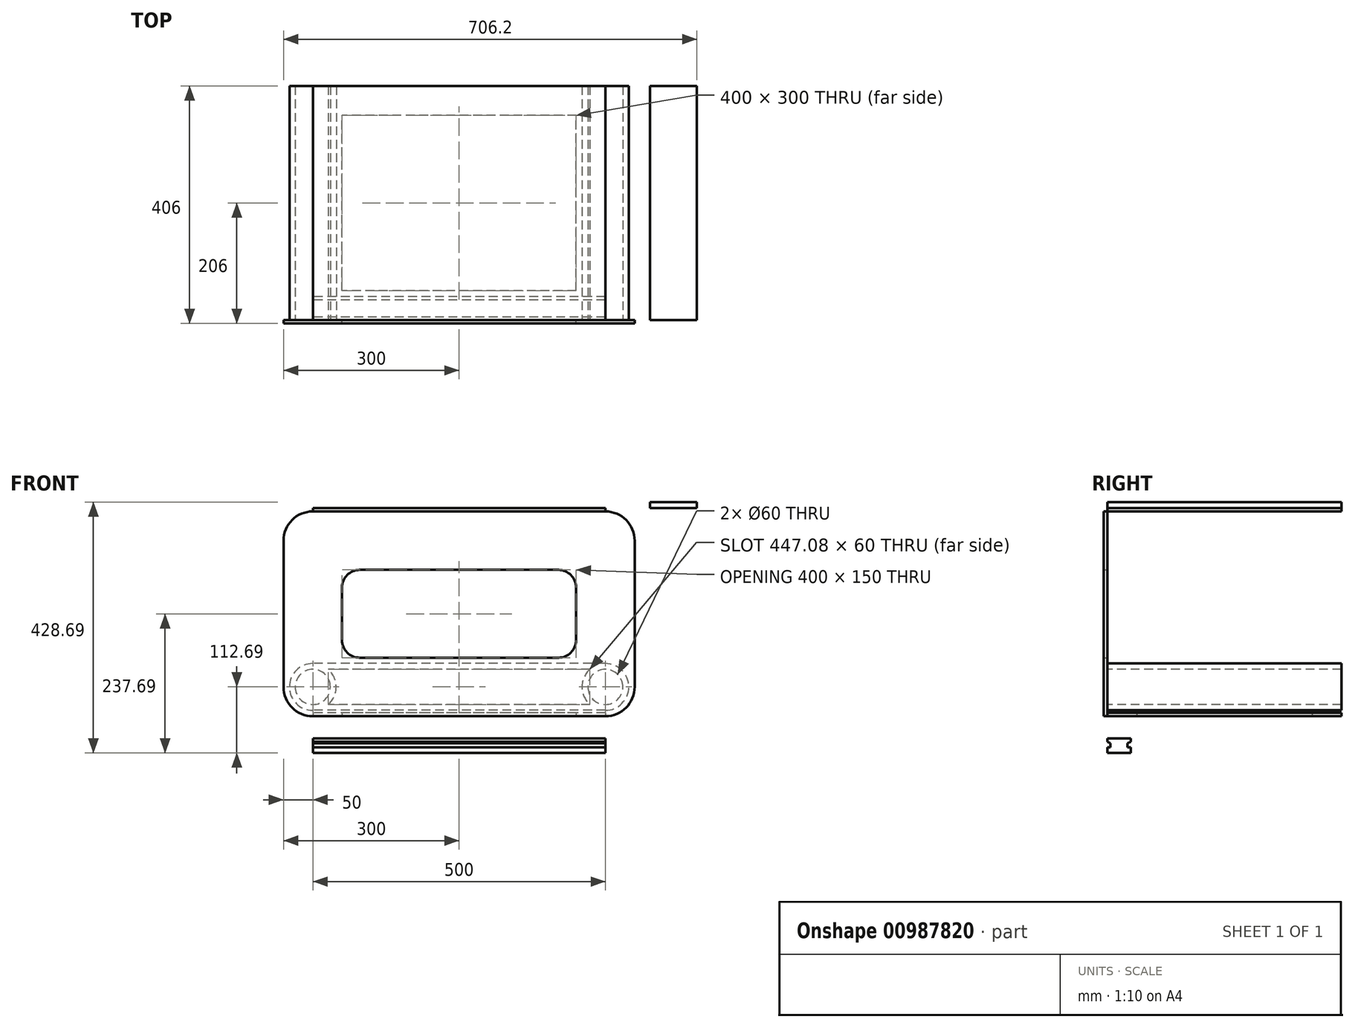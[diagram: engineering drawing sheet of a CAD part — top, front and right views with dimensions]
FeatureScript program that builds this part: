
annotation { "Feature Type Name" : "Feature", "Feature Type Description" : "" }
export const myFeature = defineFeature(function(context is Context, id is Id, definition is map)
    precondition{}
    {
        {
            var Q0;
            Q0=qCreatedBy(makeId("Front.planeOp"),FACE);
            var sketch = newSketch(context, id + "F0", { "sketchPlane" : qUnion([Q0])});
            skLineSegment(sketch, "E0", {"start": v(0, 0) * mm, "end": v(0, 175) * mm});
            skLineSegment(sketch, "E1", {"start": v(0, 175) * mm, "end": v(300, 175) * mm});
            skLineSegment(sketch, "E2.bottom", {"start": v(300, 0) * mm, "end": v(-300, 0) * mm});
            skLineSegment(sketch, "E2.top", {"start": v(300, 350) * mm, "end": v(-300, 350) * mm});
            skLineSegment(sketch, "E2.left", {"start": v(300, 0) * mm, "end": v(300, 350) * mm});
            skLineSegment(sketch, "E2.right", {"start": v(-300, 0) * mm, "end": v(-300, 350) * mm});
            skPoint(sketch, "E2.middle", {"position": v(0, 175) * mm});
            skLineSegment(sketch, "E3.bottom", {"start": v(200, 100) * mm, "end": v(-200, 100) * mm});
            skLineSegment(sketch, "E3.top", {"start": v(200, 250) * mm, "end": v(-200, 250) * mm});
            skLineSegment(sketch, "E3.left", {"start": v(200, 100) * mm, "end": v(200, 250) * mm});
            skLineSegment(sketch, "E3.right", {"start": v(-200, 100) * mm, "end": v(-200, 250) * mm});
            skSolve(sketch);
        }
        {
            var Q0;
            {var subQ0=sQuery(id+"F0.wireOp",EDGE,"E2.top");Q0=makeQuery(id+"F0.imprint","IMPRINT",FACE,{"disambiguationData":[TD([[makeQuery(id+"F0.imprint","IMPRINT",EDGE,{"derivedFrom":subQ0}),1.0]])]});}
            var Q1;
            {var subQ3=sQuery(id+"F0.wireOp",EDGE,"E2.bottom");var subQ5=sQuery(id+"F0.wireOp",EDGE,"E0");var subQ6=makeQuery(id+"F0.imprint","INTERSECT",VERTEX,{"derivedFrom":[subQ5,subQ3]});Q1=makeQuery(id+"F0.imprint","IMPRINT",FACE,{"disambiguationData":[TD([[makeQuery(id+"F0.imprint","IMPRINT",EDGE,{"disambiguationData":[TD([[subQ6,-1.0]])],"derivedFrom":subQ5}),-1.0]])]});}
            extrude(context, id + "F1", {"entities" : qUnion([Q0, Q1]), "depth" : 6 * mm, "offsetDistance" : 25 * mm});
        }
        {
            var Q0;
            Q0=makeQuery(id+"F1.opExtrude","SWEPT_EDGE",EDGE,{"disambiguationData":[OSD([sQuery(id+"F0.wireOp",EDGE,"E2.top"),sQuery(id+"F0.wireOp",EDGE,"E2.right")])]});
            var Q1;
            Q1=makeQuery(id+"F1.opExtrude","SWEPT_EDGE",EDGE,{"disambiguationData":[OSD([sQuery(id+"F0.wireOp",EDGE,"E2.bottom"),sQuery(id+"F0.wireOp",EDGE,"E2.right")])]});
            var Q2;
            Q2=makeQuery(id+"F1.opExtrude","SWEPT_EDGE",EDGE,{"disambiguationData":[OSD([sQuery(id+"F0.wireOp",EDGE,"E2.top"),sQuery(id+"F0.wireOp",EDGE,"E2.left")])]});
            var Q3;
            Q3=makeQuery(id+"F1.opExtrude","SWEPT_EDGE",EDGE,{"disambiguationData":[OSD([sQuery(id+"F0.wireOp",EDGE,"E2.bottom"),sQuery(id+"F0.wireOp",EDGE,"E2.left")])]});
            fillet(context, id + "F2", {"entities" : qUnion([Q0, Q1, Q2, Q3]), "radius" : 50 * mm, "tangentPropagation" : true, "allowEdgeOverflow" : false});
        }
        {
            var Q0;
            Q0=makeQuery(id+"F1.opExtrude","SWEPT_EDGE",EDGE,{"disambiguationData":[OSD([sQuery(id+"F0.wireOp",EDGE,"E3.top"),sQuery(id+"F0.wireOp",EDGE,"E3.right")])]});
            var Q1;
            Q1=makeQuery(id+"F1.opExtrude","SWEPT_EDGE",EDGE,{"disambiguationData":[OSD([sQuery(id+"F0.wireOp",EDGE,"E3.bottom"),sQuery(id+"F0.wireOp",EDGE,"E3.right")])]});
            var Q2;
            Q2=makeQuery(id+"F1.opExtrude","SWEPT_EDGE",EDGE,{"disambiguationData":[OSD([sQuery(id+"F0.wireOp",EDGE,"E3.top"),sQuery(id+"F0.wireOp",EDGE,"E3.left")])]});
            var Q3;
            Q3=makeQuery(id+"F1.opExtrude","SWEPT_EDGE",EDGE,{"disambiguationData":[OSD([sQuery(id+"F0.wireOp",EDGE,"E3.bottom"),sQuery(id+"F0.wireOp",EDGE,"E3.left")])]});
            fillet(context, id + "F3", {"entities" : qUnion([Q0, Q1, Q2, Q3]), "radius" : 30 * mm, "tangentPropagation" : true, "allowEdgeOverflow" : false});
        }
        {
            var Q0;
            Q0=qCreatedBy(makeId("Top.planeOp"),FACE);
            var sketch = newSketch(context, id + "F4", { "sketchPlane" : qUnion([Q0])});
            skLineSegment(sketch, "E4", {"start": v(0, 0) * mm, "end": v(0, 200) * mm});
            skLineSegment(sketch, "E5", {"start": v(0, 200) * mm, "end": v(250, 200) * mm});
            skLineSegment(sketch, "E6", {"start": v(250, 200) * mm, "end": v(250, 0) * mm});
            skLineSegment(sketch, "E7.bottom", {"start": v(250, 0) * mm, "end": v(-250, 0) * mm});
            skLineSegment(sketch, "E7.top", {"start": v(250, 400) * mm, "end": v(-250, 400) * mm});
            skLineSegment(sketch, "E7.left", {"start": v(250, 0) * mm, "end": v(250, 400) * mm});
            skLineSegment(sketch, "E7.right", {"start": v(-250, 0) * mm, "end": v(-250, 400) * mm});
            skPoint(sketch, "E7.middle", {"position": v(0, 200) * mm});
            skLineSegment(sketch, "E8.bottom", {"start": v(200, 50) * mm, "end": v(-200, 50) * mm});
            skLineSegment(sketch, "E8.top", {"start": v(200, 350) * mm, "end": v(-200, 350) * mm});
            skLineSegment(sketch, "E8.left", {"start": v(200, 50) * mm, "end": v(200, 350) * mm});
            skLineSegment(sketch, "E8.right", {"start": v(-200, 50) * mm, "end": v(-200, 350) * mm});
            skSolve(sketch);
        }
        {
            var Q0;
            {var subQ0=sQuery(id+"F4.wireOp",EDGE,"E7.top");Q0=makeQuery(id+"F4.imprint","IMPRINT",FACE,{"disambiguationData":[TD([[makeQuery(id+"F4.imprint","IMPRINT",EDGE,{"derivedFrom":subQ0}),1.0]])]});}
            var Q1;
            {var subQ3=sQuery(id+"F4.wireOp",EDGE,"E7.bottom");var subQ5=sQuery(id+"F4.wireOp",EDGE,"E4");var subQ6=makeQuery(id+"F4.imprint","INTERSECT",VERTEX,{"derivedFrom":[subQ5,subQ3]});Q1=makeQuery(id+"F4.imprint","IMPRINT",FACE,{"disambiguationData":[TD([[makeQuery(id+"F4.imprint","IMPRINT",EDGE,{"disambiguationData":[TD([[subQ6,-1.0]])],"derivedFrom":subQ5}),-1.0]])]});}
            extrude(context, id + "F5", {"entities" : qUnion([Q0, Q1]), "depth" : 6 * mm, "offsetDistance" : 25 * mm});
        }
        {
            var Q0;
            Q0=makeQuery(id+"F1.opExtrude","SWEPT_FACE",FACE,{"disambiguationData":[OSD([sQuery(id+"F0.wireOp",EDGE,"E2.top")])]});
            var sketch = newSketch(context, id + "F6", { "sketchPlane" : qUnion([Q0])});
            skLineSegment(sketch, "E9", {"start": v(0, 0) * mm, "end": v(0, 200) * mm});
            skLineSegment(sketch, "E10", {"start": v(0, 200) * mm, "end": v(250, 200) * mm});
            skLineSegment(sketch, "E11.bottom", {"start": v(250, 0) * mm, "end": v(-250, 0) * mm});
            skLineSegment(sketch, "E11.top", {"start": v(250, 400) * mm, "end": v(-250, 400) * mm});
            skLineSegment(sketch, "E11.left", {"start": v(250, 0) * mm, "end": v(250, 400) * mm});
            skLineSegment(sketch, "E11.right", {"start": v(-250, 0) * mm, "end": v(-250, 400) * mm});
            skPoint(sketch, "E11.middle", {"position": v(0, 200) * mm});
            skSolve(sketch);
        }
        {
            var Q0;
            {var subQ4=sQuery(id+"F6.wireOp",EDGE,"E9");Q0=makeQuery(id+"F6.imprint","IMPRINT",FACE,{"disambiguationData":[TD([[makeQuery(id+"F6.imprint","IMPRINT",EDGE,{"derivedFrom":subQ4}),1.0]])]});}
            var Q1;
            {var subQ0=sQuery(id+"F6.wireOp",EDGE,"E9");Q1=makeQuery(id+"F6.imprint","IMPRINT",FACE,{"disambiguationData":[TD([[makeQuery(id+"F6.imprint","IMPRINT",EDGE,{"derivedFrom":subQ0}),-1.0]])]});}
            extrude(context, id + "F7", {"entities" : qUnion([Q0, Q1]), "depth" : 6 * mm, "offsetDistance" : 25 * mm});
        }
        {
            var Q0;
            Q0=makeQuery(id+"F1.opExtrude","CAP_FACE",FACE,{"disambiguationData":[OSD([sQuery(id+"F0.wireOp",EDGE,"E2.bottom"),sQuery(id+"F0.wireOp",EDGE,"E2.top"),sQuery(id+"F0.wireOp",EDGE,"E2.left"),sQuery(id+"F0.wireOp",EDGE,"E2.right"),sQuery(id+"F0.wireOp",EDGE,"E3.bottom"),sQuery(id+"F0.wireOp",EDGE,"E3.top"),sQuery(id+"F0.wireOp",EDGE,"E3.left"),sQuery(id+"F0.wireOp",EDGE,"E3.right")])],"isStart":true});
            var sketch = newSketch(context, id + "F8", { "sketchPlane" : qUnion([Q0])});
            skArc(sketch, "E12", {"start": v(-250, 90) * mm, "mid": v(-290, 50) * mm, "end": v(-250, 10) * mm});
            skArc(sketch, "E13", {"start": v(223.54, 80) * mm, "mid": v(210, 50) * mm, "end": v(223.54, 20) * mm});
            skLineSegment(sketch, "E14", {"start": v(-250, 90) * mm, "end": v(250, 90) * mm});
            skLineSegment(sketch, "E15", {"start": v(-250, 10) * mm, "end": v(250, 10) * mm});
            skCircle(sketch, "E16", {"center": v(-250, 50) * mm, "radius": 30 * mm});
            skCircle(sketch, "E17", {"center": v(250, 50) * mm, "radius": 30 * mm});
            skLineSegment(sketch, "E18", {"start": v(-223.54, 80) * mm, "end": v(223.54, 80) * mm});
            skLineSegment(sketch, "E19", {"start": v(-223.54, 20) * mm, "end": v(223.54, 20) * mm});
            skPoint(sketch, "E20.orphan", {"position": v(-250, 80) * mm});
            skPoint(sketch, "E21.orphan", {"position": v(-250, 20) * mm});
            skArc(sketch, "E22.trimOffspring", {"start": v(-223.54, 20) * mm, "mid": v(-210, 50) * mm, "end": v(-223.54, 80) * mm});
            skPoint(sketch, "E23.orphan", {"position": v(250, 80) * mm});
            skPoint(sketch, "E24.orphan", {"position": v(250, 20) * mm});
            skArc(sketch, "E25.trimOffspring", {"start": v(250, 10) * mm, "mid": v(290, 50) * mm, "end": v(250, 90) * mm});
            skSolve(sketch);
        }
        {
            var Q0;
            Q0 = qSketchRegion(id + "F8", true);
            extrude(context, id + "F9", {"entities" : qUnion([Q0]), "depth" : 400 * mm, "offsetDistance" : 25 * mm});
        }
        {
            var Q0;
            Q0=qCreatedBy(makeId("Right.planeOp"),FACE);
            var sketch = newSketch(context, id + "F10", { "sketchPlane" : qUnion([Q0])});
            skLineSegment(sketch, "E26.bottom", {"start": v(0, -37.69) * mm, "end": v(40, -37.69) * mm});
            skLineSegment(sketch, "E26.top", {"start": v(0, -62.69) * mm, "end": v(40, -62.69) * mm});
            skLineSegment(sketch, "E26.left", {"start": v(0, -37.69) * mm, "end": v(0, -43.38) * mm});
            skLineSegment(sketch, "E26.right", {"start": v(40, -37.69) * mm, "end": v(40, -43.38) * mm});
            skLineSegment(sketch, "E27", {"start": v(40, -43.38) * mm, "end": v(34.58, -46.3) * mm});
            skLineSegment(sketch, "E28", {"start": v(34.58, -46.3) * mm, "end": v(34.58, -53.11) * mm});
            skLineSegment(sketch, "E29", {"start": v(34.58, -53.11) * mm, "end": v(40, -53.11) * mm});
            skLineSegment(sketch, "E30.trimOffspring", {"start": v(40, -53.11) * mm, "end": v(40, -62.69) * mm});
            skPoint(sketch, "E31.startSnap0", {"position": v(20, -37.69) * mm});
            skLineSegment(sketch, "E32.MirrorCS", {"start": v(0, -43.38) * mm, "end": v(5.42, -46.3) * mm});
            skLineSegment(sketch, "E33.MirrorCS", {"start": v(5.42, -46.3) * mm, "end": v(5.42, -53.11) * mm});
            skLineSegment(sketch, "E34.MirrorCS", {"start": v(5.42, -53.11) * mm, "end": v(0, -53.11) * mm});
            skLineSegment(sketch, "E35.trimOffspring", {"start": v(0, -53.11) * mm, "end": v(0, -62.69) * mm});
            skSolve(sketch);
        }
        {
            var Q0;
            Q0 = qSketchRegion(id + "F10", true);
            extrude(context, id + "F11", {"entities" : qUnion([Q0]), "depth" : 250 * mm, "offsetDistance" : 25 * mm, "hasSecondDirection" : true, "secondDirectionOppositeDirection" : true, "secondDirectionDepth" : 250 * mm});
        }
        {
            var Q0;
            Q0=makeQuery(id+"F7.opExtrude","CAP_FACE",FACE,{"disambiguationData":[OSD([sQuery(id+"F6.wireOp",EDGE,"E11.bottom"),sQuery(id+"F6.wireOp",EDGE,"E11.top"),sQuery(id+"F6.wireOp",EDGE,"E11.left"),sQuery(id+"F6.wireOp",EDGE,"E11.right")])],"isStart":false});
            var sketch = newSketch(context, id + "F12", { "sketchPlane" : qUnion([Q0])});
            skLineSegment(sketch, "E36", {"start": v(250, 200) * mm, "end": v(481.49, 200) * mm});
            skLineSegment(sketch, "E37", {"start": v(481.49, 200) * mm, "end": v(406.2, 200) * mm});
            skLineSegment(sketch, "E38", {"start": v(406.2, 200) * mm, "end": v(406.2, 400) * mm});
            skLineSegment(sketch, "E39", {"start": v(406.2, 200) * mm, "end": v(406.2, 0) * mm});
            skLineSegment(sketch, "E40", {"start": v(406.2, 400) * mm, "end": v(326.2, 400) * mm});
            skLineSegment(sketch, "E41", {"start": v(326.2, 400) * mm, "end": v(326.2, 0) * mm});
            skLineSegment(sketch, "E42", {"start": v(326.2, 0) * mm, "end": v(406.2, 0) * mm});
            skSolve(sketch);
        }
        {
            var Q0;
            {var subQ0=sQuery(id+"F12.wireOp",EDGE,"E38");Q0=makeQuery(id+"F12.imprint","IMPRINT",FACE,{"disambiguationData":[TD([[makeQuery(id+"F12.imprint","IMPRINT",EDGE,{"derivedFrom":subQ0}),1.0]])]});}
            var Q1;
            {var subQ0=sQuery(id+"F12.wireOp",EDGE,"E39");Q1=makeQuery(id+"F12.imprint","IMPRINT",FACE,{"disambiguationData":[TD([[makeQuery(id+"F12.imprint","IMPRINT",EDGE,{"derivedFrom":subQ0}),-1.0]])]});}
            extrude(context, id + "F13", {"entities" : qUnion([Q0, Q1]), "depth" : 10 * mm, "offsetDistance" : 25 * mm});
        }
    });
